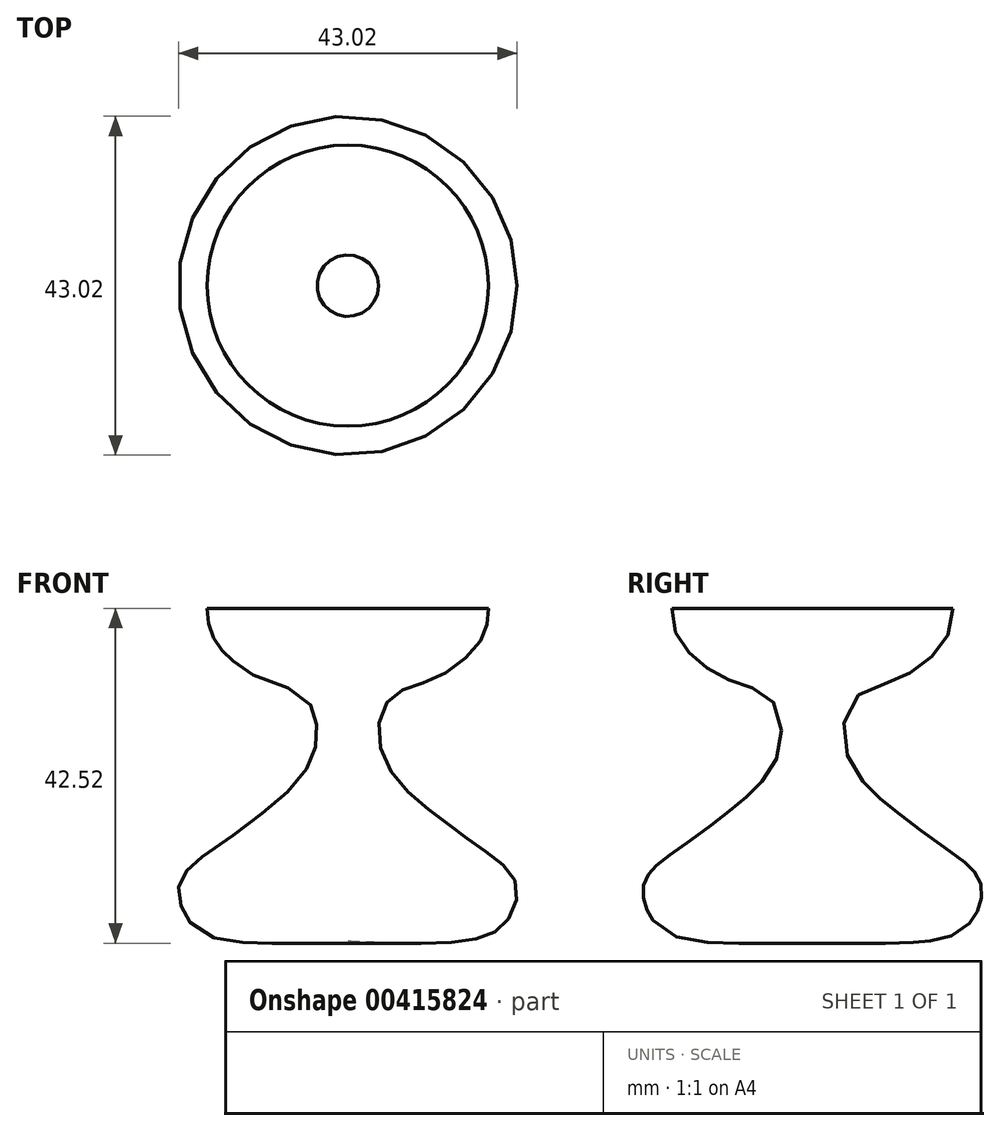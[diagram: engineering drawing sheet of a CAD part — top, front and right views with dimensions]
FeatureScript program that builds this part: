
annotation { "Feature Type Name" : "Feature", "Feature Type Description" : "" }
export const myFeature = defineFeature(function(context is Context, id is Id, definition is map)
    precondition{}
    {
        {
            var Q0;
            Q0=qCreatedBy(makeId("Front.planeOp"),FACE);
            var sketch = newSketch(context, id + "F0", { "sketchPlane" : qUnion([Q0])});
            skFitSpline(sketch, "E0", {"points": [v(0, 0) * mm, v(14.9, 0) * mm, v(20, 2.28) * mm, v(21.34, 7.37) * mm, v(17.05, 11.66) * mm, v(10.89, 16.22) * mm, v(4.45, 23.46) * mm, v(5.26, 30.7) * mm, v(11.16, 33.38) * mm, v(17.05, 38.48) * mm, v(17.86, 42.23) * mm], "startDerivative": vector(116.31, -5.23) * mm, "endDerivative": vector(1.73, 49.98) * mm});
            skLineSegment(sketch, "E1", {"start": v(0, 0) * mm, "end": v(0, 58.7) * mm, "construction": true});
            skSolve(sketch);
        }
        {
            var Q0;
            Q0 = qSketchRegion(id + "F0", true);
            var Q1;
            Q1=sQuery(id+"F0.wireOp",EDGE,"E0");
            var Q2;
            Q2=sQuery(id+"F0.wireOp",EDGE,"E1");
            revolve(context, id + "F1", {"bodyType" : ToolBodyType.SURFACE, "entities" : qUnion([Q0]), "surfaceEntities" : qUnion([Q1]), "axis" : qUnion([Q2]), "revolveType" : RevolveType.FULL});
        }
    });
